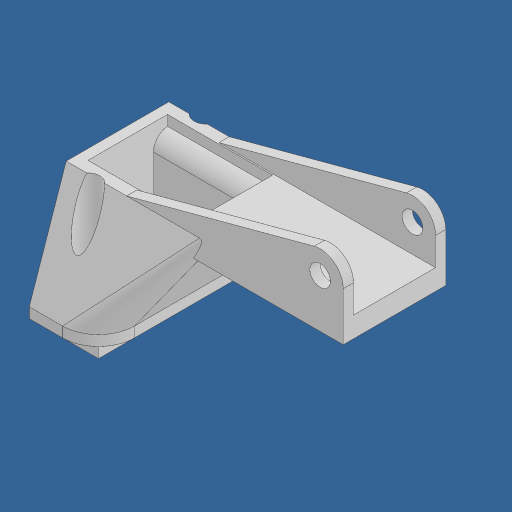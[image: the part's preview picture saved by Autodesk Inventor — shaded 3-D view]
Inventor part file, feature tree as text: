
AUTODESK INVENTOR PART (.ipt)
format: ipt  version: 2024.2 (Build 282272000, 272)  size: 237,568 bytes
history: native  units: mm
features: sketch x8, extrude x6, plane x1, loft x1, hole x1, mirror x1, fillet x1, other x1
ambient origin geometry x8: Origin, YZ Plane, XZ Plane, XY Plane, X Axis, Y Axis, Z Axis, Center Point
bodies: Solid1 (feature_tree)
feature tree (20):
  extrude  "Extrusion1"  Depth=30.4mm
  extrude  "Extrusion2"  Depth=2.0mm
  plane  "Work Plane1"
  loft  "Loft1"
  extrude  "Extrusion3"  Depth=2.0mm
  hole  "Hole1"  [1 undecoded]
  extrude  "Extrusion4"  TaperAngle=0.0deg  [1 undecoded]
  extrude  "Extrusion6"  TaperAngle=0.0deg  [1 undecoded]
  extrude  "Extrusion7"  Depth=2.0mm
  mirror  "Mirror1"
  fillet  "Fillet1"  Radius=10.0mm
  sketch  "Sketch1"  dims[d0=11.5mm d1=30.4mm]
  sketch  "Sketch2"  dims[d2=2.0mm d3=0.0mm d4=2.0mm]
  sketch  "Sketch3"  dims[d5=2.0mm d6=2.0mm]
  other  "Edges1"
  sketch  "Sketch4"  dims[d7=2.0mm d8=0.0mm d9=25.0mm]
  sketch  "Sketch5"  dims[d10=20.0mm d11=28.0mm]
  sketch  "Sketch6"  dims[d12=0.0mm d13=90.0deg d14=0.0mm d15=90.0deg]
  sketch  "Sketch8"  dims[d16=20.5mm d17=0.0mm]
  sketch  "Sketch10"  dims[d18=2.0mm d19=2.0mm d20=10.0mm d21=0.0mm d22=11.5mm d23=11.5mm d24=4.6mm d25=6.0mm d26=6.3mm d27=2.0mm d28=90.0deg d29=6.0mm d30=20.594885mm d32=2.0mm d33=0.0mm d44=4.0mm d45=20.0mm d46=0.0mm d47=54.0mm d48=4.0mm d49=5.45mm d50=4.5mm d51=4.5mm d52=2.0mm d53=0.0mm d57=15.0deg d58=7.0mm d59=2.0mm d60=45.0deg d61=15.5mm d62=3.0mm]
note: 3 required parameter values undecoded (feature->parameter linkage not recoverable at this tier; creation-order binding heuristic only, values carry confidence <= 0.55)
